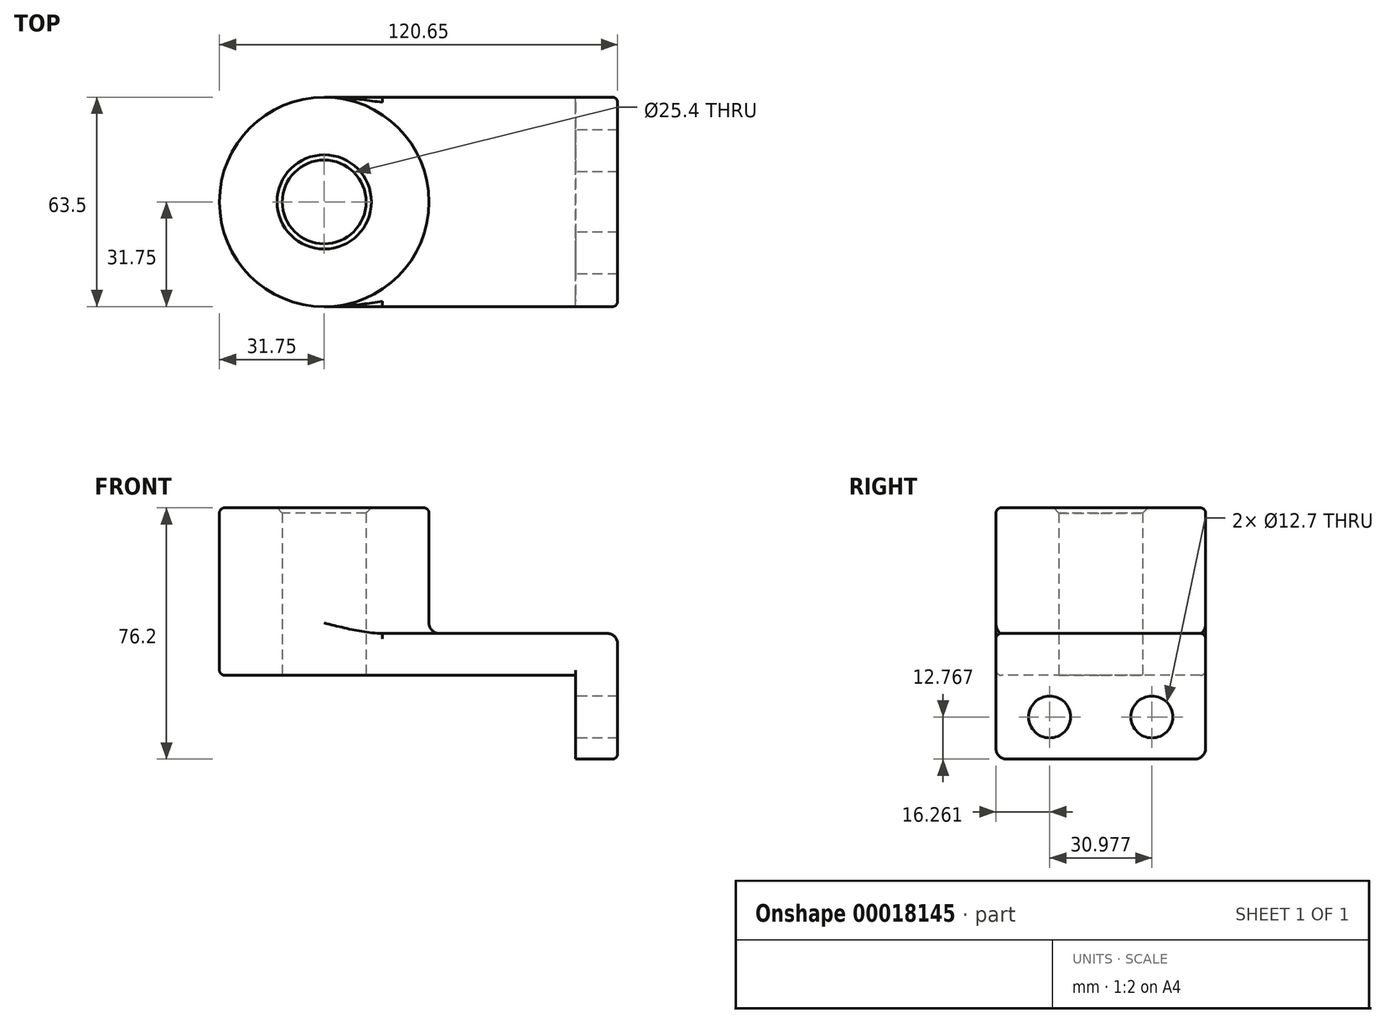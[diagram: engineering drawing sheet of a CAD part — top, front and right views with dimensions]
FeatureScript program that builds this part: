
annotation { "Feature Type Name" : "Feature", "Feature Type Description" : "" }
export const myFeature = defineFeature(function(context is Context, id is Id, definition is map)
    precondition{}
    {
        {
            var Q0;
            Q0=qCreatedBy(makeId("Top.planeOp"),FACE);
            var sketch = newSketch(context, id + "F0", { "sketchPlane" : qUnion([Q0])});
            skLineSegment(sketch, "E0.rect.bottom", {"start": v(-38.1, 31.75) * mm, "end": v(38.1, 31.75) * mm});
            skLineSegment(sketch, "E0.rect.top", {"start": v(-38.1, -31.75) * mm, "end": v(38.1, -31.75) * mm});
            skLineSegment(sketch, "E0.rect.left", {"start": v(-38.1, 31.75) * mm, "end": v(-38.1, -31.75) * mm});
            skLineSegment(sketch, "E0.rect.right", {"start": v(38.1, 31.75) * mm, "end": v(38.1, -31.75) * mm});
            skPoint(sketch, "E0.rect.middle", {"position": v(0, 0) * mm});
            skCircle(sketch, "E1", {"center": v(-38.1, 0) * mm, "radius": 31.75 * mm});
            skCircle(sketch, "E2", {"center": v(-38.1, 0) * mm, "radius": 12.7 * mm});
            skSolve(sketch);
        }
        {
            var Q0;
            {var subQ3=sQuery(id+"F0.wireOp",EDGE,"E0.rect.bottom");Q0=makeQuery(id+"F0.imprint","IMPRINT",FACE,{"disambiguationData":[TD([[makeQuery(id+"F0.imprint","IMPRINT",EDGE,{"derivedFrom":subQ3}),-1.0]])]});}
            var Q1;
            {var subQ0=sQuery(id+"F0.wireOp",EDGE,"E2");var subQ1=sQuery(id+"F0.wireOp",EDGE,"E0.rect.left");var subQ3=makeQuery(id+"F0.imprint","INTERSECT",VERTEX,{"disambiguationData":[OD(0.0)],"derivedFrom":[subQ1,subQ0]});Q1=makeQuery(id+"F0.imprint","IMPRINT",FACE,{"disambiguationData":[TD([[makeQuery(id+"F0.imprint","IMPRINT",EDGE,{"disambiguationData":[TD([[subQ3,-1.0]])],"derivedFrom":subQ0}),-1.0]])]});}
            var Q2;
            {var subQ0=sQuery(id+"F0.wireOp",EDGE,"E2");var subQ1=sQuery(id+"F0.wireOp",EDGE,"E0.rect.left");var subQ3=makeQuery(id+"F0.imprint","INTERSECT",VERTEX,{"disambiguationData":[OD(0.0)],"derivedFrom":[subQ1,subQ0]});Q2=makeQuery(id+"F0.imprint","IMPRINT",FACE,{"disambiguationData":[TD([[makeQuery(id+"F0.imprint","IMPRINT",EDGE,{"disambiguationData":[TD([[subQ3,1.0]])],"derivedFrom":subQ0}),-1.0]])]});}
            extrude(context, id + "F1", {"entities" : qUnion([Q0, Q1, Q2]), "depth" : 12.7 * mm});
        }
        {
            var Q0;
            {var subQ0=sQuery(id+"F0.wireOp",EDGE,"E2");var subQ1=sQuery(id+"F0.wireOp",EDGE,"E0.rect.left");var subQ3=makeQuery(id+"F0.imprint","INTERSECT",VERTEX,{"disambiguationData":[OD(0.0)],"derivedFrom":[subQ1,subQ0]});Q0=makeQuery(id+"F0.imprint","IMPRINT",FACE,{"disambiguationData":[TD([[makeQuery(id+"F0.imprint","IMPRINT",EDGE,{"disambiguationData":[TD([[subQ3,-1.0]])],"derivedFrom":subQ0}),-1.0]])]});}
            var Q1;
            {var subQ0=sQuery(id+"F0.wireOp",EDGE,"E2");var subQ1=sQuery(id+"F0.wireOp",EDGE,"E0.rect.left");var subQ3=makeQuery(id+"F0.imprint","INTERSECT",VERTEX,{"disambiguationData":[OD(0.0)],"derivedFrom":[subQ1,subQ0]});Q1=makeQuery(id+"F0.imprint","IMPRINT",FACE,{"disambiguationData":[TD([[makeQuery(id+"F0.imprint","IMPRINT",EDGE,{"disambiguationData":[TD([[subQ3,1.0]])],"derivedFrom":subQ0}),-1.0]])]});}
            extrude(context, id + "F2", {"entities" : qUnion([Q0, Q1]), "operationType" : NewBodyOperationType.ADD, "depth" : 50.8 * mm});
        }
        {
            var Q0;
            Q0=makeQuery(id+"F1.opExtrude","SWEPT_FACE",FACE,{"disambiguationData":[OSD([sQuery(id+"F0.wireOp",EDGE,"E0.rect.right")])]});
            var sketch = newSketch(context, id + "F3", { "sketchPlane" : qUnion([Q0])});
            skLineSegment(sketch, "E3.bottom", {"start": v(-31.75, 12.7) * mm, "end": v(31.75, 12.7) * mm});
            skLineSegment(sketch, "E3.top", {"start": v(-31.75, -25.4) * mm, "end": v(31.75, -25.4) * mm});
            skLineSegment(sketch, "E3.left", {"start": v(-31.75, 12.7) * mm, "end": v(-31.75, -25.4) * mm});
            skLineSegment(sketch, "E3.right", {"start": v(31.75, 12.7) * mm, "end": v(31.75, -25.4) * mm});
            skLineSegment(sketch, "E4", {"start": v(0, 0) * mm, "end": v(0, -25.4) * mm});
            skCircle(sketch, "E5", {"center": v(-15.49, -12.63) * mm, "radius": 6.35 * mm});
            skCircle(sketch, "E6.MirrorC", {"center": v(15.49, -12.63) * mm, "radius": 6.35 * mm});
            skSolve(sketch);
        }
        {
            var Q0;
            Q0 = qSketchRegion(id + "F3", true);
            extrude(context, id + "F4", {"entities" : qUnion([Q0]), "operationType" : NewBodyOperationType.ADD, "depth" : 12.7 * mm});
        }
        {
            var Q0;
            {var subQ0=sQuery(id+"F0.wireOp",EDGE,"E1");Q0=makeQuery(id+"F2.boolean.opBoolean","INTERSECT",EDGE,{"derivedFrom":[makeQuery(id+"F1.opExtrude","CAP_FACE",FACE,{"disambiguationData":[OSD([sQuery(id+"F0.wireOp",EDGE,"E0.rect.bottom"),sQuery(id+"F0.wireOp",EDGE,"E0.rect.top"),sQuery(id+"F0.wireOp",EDGE,"E0.rect.right"),subQ0,sQuery(id+"F0.wireOp",EDGE,"E2")])],"isStart":false}),makeQuery(id+"F2.opExtrude","SWEPT_FACE",FACE,{"disambiguationData":[OSD([subQ0])]})]});}
            var Q1;
            Q1=makeQuery(id+"F4.opExtrude","CAP_EDGE",EDGE,{"disambiguationData":[OSD([sQuery(id+"F3.wireOp",EDGE,"E3.bottom")])],"isStart":false});
            var Q2;
            Q2=makeQuery(id+"F4.opExtrude","SWEPT_EDGE",EDGE,{"disambiguationData":[OSD([sQuery(id+"F3.wireOp",EDGE,"E3.top"),sQuery(id+"F3.wireOp",EDGE,"E3.left")])]});
            var Q3;
            Q3=makeQuery(id+"F4.opExtrude","SWEPT_EDGE",EDGE,{"disambiguationData":[OSD([sQuery(id+"F3.wireOp",EDGE,"E3.top"),sQuery(id+"F3.wireOp",EDGE,"E3.right")])]});
            fillet(context, id + "F5", {"entities" : qUnion([Q0, Q1, Q2, Q3]), "radius" : 3.17 * mm, "tangentPropagation" : true, "allowEdgeOverflow" : false});
        }
        {
            var Q0;
            Q0=makeQuery(id+"F2.opExtrude","CAP_EDGE",EDGE,{"disambiguationData":[OSD([sQuery(id+"F0.wireOp",EDGE,"E2")])],"isStart":false});
            chamfer(context, id + "F6", {"entities" : qUnion([Q0]), "width" : 1.59 * mm, "tangentPropagation" : true});
        }
        {
            var Q0;
            Q0=makeQuery(id+"F1.opExtrude","CAP_EDGE",EDGE,{"disambiguationData":[OSD([sQuery(id+"F0.wireOp",EDGE,"E1")])],"isStart":true});
            var Q1;
            Q1=makeQuery(id+"F1.opExtrude","CAP_EDGE",EDGE,{"disambiguationData":[OSD([sQuery(id+"F0.wireOp",EDGE,"E0.rect.bottom")])],"isStart":true});
            var Q2;
            Q2=makeQuery(id+"F1.opExtrude","CAP_EDGE",EDGE,{"disambiguationData":[OSD([sQuery(id+"F0.wireOp",EDGE,"E0.rect.top")])],"isStart":true});
            fillet(context, id + "F7", {"entities" : qUnion([Q0, Q1, Q2]), "radius" : 1.59 * mm, "tangentPropagation" : true, "allowEdgeOverflow" : false});
        }
        {
            var Q0;
            Q0=makeQuery(id+"F4.boolean.opBoolean","MERGE",EDGE,{"derivedFrom":[makeQuery(id+"F1.opExtrude","CAP_EDGE",EDGE,{"disambiguationData":[OSD([sQuery(id+"F0.wireOp",EDGE,"E0.rect.top")])],"isStart":false}),makeQuery(id+"F4.opExtrude","SWEPT_EDGE",EDGE,{"disambiguationData":[OSD([sQuery(id+"F3.wireOp",EDGE,"E3.bottom"),sQuery(id+"F3.wireOp",EDGE,"E3.left")])]})]});
            var Q1;
            Q1=makeQuery(id+"F4.opExtrude","CAP_EDGE",EDGE,{"disambiguationData":[OSD([sQuery(id+"F3.wireOp",EDGE,"E3.left")])],"isStart":false});
            var Q2;
            Q2=makeQuery(id+"F4.opExtrude","CAP_EDGE",EDGE,{"disambiguationData":[OSD([sQuery(id+"F3.wireOp",EDGE,"E3.right")])],"isStart":false});
            var Q3;
            Q3=makeQuery(id+"F4.boolean.opBoolean","MERGE",EDGE,{"derivedFrom":[makeQuery(id+"F1.opExtrude","CAP_EDGE",EDGE,{"disambiguationData":[OSD([sQuery(id+"F0.wireOp",EDGE,"E0.rect.bottom")])],"isStart":false}),makeQuery(id+"F4.opExtrude","SWEPT_EDGE",EDGE,{"disambiguationData":[OSD([sQuery(id+"F3.wireOp",EDGE,"E3.bottom"),sQuery(id+"F3.wireOp",EDGE,"E3.right")])]})]});
            fillet(context, id + "F8", {"entities" : qUnion([Q0, Q1, Q2, Q3]), "radius" : 1.59 * mm, "tangentPropagation" : true, "allowEdgeOverflow" : false});
        }
        {
            var Q0;
            Q0=makeQuery(id+"F2.opExtrude","CAP_EDGE",EDGE,{"disambiguationData":[OSD([sQuery(id+"F0.wireOp",EDGE,"E1")])],"isStart":false});
            fillet(context, id + "F9", {"entities" : qUnion([Q0]), "radius" : 1.59 * mm, "tangentPropagation" : true, "allowEdgeOverflow" : false});
        }
    });
